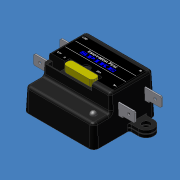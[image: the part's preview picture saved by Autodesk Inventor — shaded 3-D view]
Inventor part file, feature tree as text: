
AUTODESK INVENTOR PART (.ipt)
format: ipt  version: 2012 (Build 160160000, 160)  size: 629,248 bytes
history: native  units: mm (DEFAULTED — no unit token found)
features: sketch x19, extrude x13, projected_geometry x5, plane x4, mirror x2, revolve x1, fillet x1, other x1
ambient origin geometry x8: Origin, YZ Plane, XZ Plane, XY Plane, X Axis, Y Axis, Z Axis, Center Point
bodies: Solid1 (feature_tree)
feature tree (46):
  extrude  "Extrusion1"  Depth=41.656mm
  plane  "Work Plane1"
  extrude  "Extrusion2"  Depth=26.035mm
  extrude  "Extrusion3"  Depth=11.43mm
  plane  "Work Plane2"
  extrude  "Extrusion4"  Depth=26.035mm TaperAngle=0.0deg
  plane  "Work Plane3"
  mirror  "Mirror1"
  extrude  "Extrusion5"  Depth=10.16mm
  revolve  "Revolution1"  [1 undecoded]
  plane  "Work Plane4"
  extrude  "Extrusion6"  Depth=1.905mm TaperAngle=0.0deg
  extrude  "Extrusion7"  Depth=1.905mm TaperAngle=0.0deg
  extrude  "Extrusion8"  TaperAngle=0.0deg  [1 undecoded]
  mirror  "Mirror2"
  extrude  "Extrusion9"  Depth=21.59mm
  extrude  "Extrusion10"  Depth=3.81mm
  extrude  "Extrusion11"  Depth=0.635mm
  extrude  "Extrusion12"  Depth=3.81mm
  extrude  "Extrusion13"  Depth=23.3045mm
  fillet  "Fillet1"  Radius=0.889mm
  sketch  "Sketch16"  dims[d35=6.35mm]
  sketch  "Sketch17"  dims[d36=0.889mm]
  sketch  "Sketch18"  dims[d37=16.51mm]
  sketch  "Sketch19"  dims[d38=10.16mm d39=0.0mm d40=10.795mm d41=0.0mm d42=1.905mm d43=2.54mm d44=6.35mm d46=8.225975mm d47=4.127233mm d48=0.635mm d49=0.635mm d50=0.635mm d51=0.635mm d52=10.795mm d53=0.0mm d54=10.795mm d55=0.0mm d56=3.175mm d57=8.255mm d58=0.0mm d60=0.0mm d61=7.239mm d62=0.0mm d63=1.27mm d64=1.27mm d65=30.0mm d67=2.54mm d68=10.0mm d70=25.4mm d72=0.9525mm d73=0.9525mm d74=0.635mm d75=-6.981317mm d76=5.08mm d77=0.889mm d78=0.0mm d79=19.05mm d80=5.08mm d81=1.905mm d82=0.889mm d83=0.0mm d84=1.524mm d86=41.91mm]
  sketch  "Sketch1"  dims[d0=46.609mm d1=41.656mm]
  sketch  "Sketch2"  dims[d2=3.175mm d3=26.035mm d4=-0.523599mm]
  sketch  "Sketch3"  dims[d5=4.6355mm d6=11.43mm]
  sketch  "Sketch4"  dims[d7=11.43mm d8=26.035mm d9=0.0mm]
  projected_geometry  "Projected Loop1"
  sketch  "Sketch5"  dims[d10=5.08mm d11=10.16mm]
  sketch  "Sketch6"  dims[d12=5.969mm d13=8.001mm]
  sketch  "Sketch7"  dims[d14=1.27mm d15=1.905mm d16=0.0mm]
  projected_geometry  "Projected Loop2"
  projected_geometry  "Projected Loop3"
  sketch  "Sketch8"  dims[d17=0.508mm d18=1.905mm d19=0.0mm]
  projected_geometry  "Projected Loop4"
  sketch  "Sketch9"  dims[d20=23.3045mm d21=0.0mm]
  sketch  "Sketch10"  dims[d22=6.985mm d23=21.59mm]
  projected_geometry  "Projected Loop5"
  sketch  "Sketch11"  dims[d24=10.795mm d25=3.81mm]
  sketch  "Sketch12"  dims[d26=0.635mm d27=0.635mm]
  sketch  "Sketch13"  dims[d28=4.191mm d29=0.0mm d30=3.81mm]
  sketch  "Sketch14"  dims[d31=90.0deg d32=23.3045mm d33=0.889mm]
  sketch  "Sketch15"  dims[d34=7.366mm]
  other  "Image1"
note: 2 required parameter values undecoded (feature->parameter linkage not recoverable at this tier; creation-order binding heuristic only, values carry confidence <= 0.55)